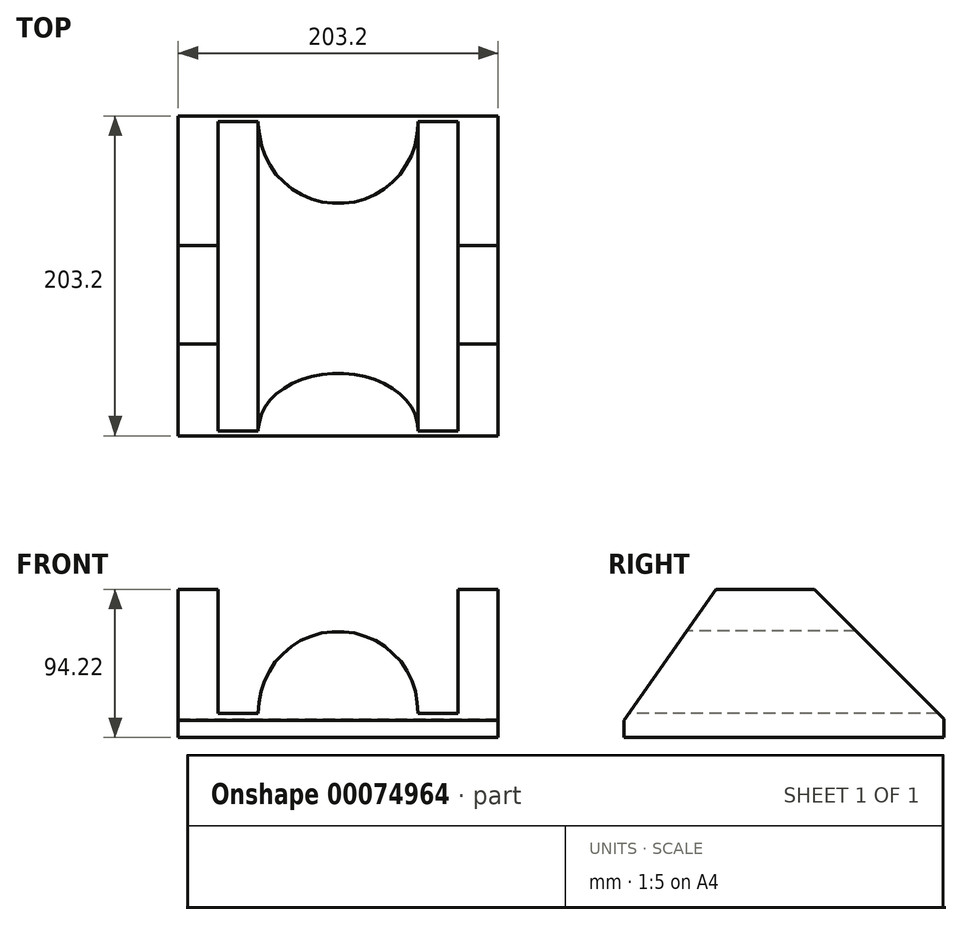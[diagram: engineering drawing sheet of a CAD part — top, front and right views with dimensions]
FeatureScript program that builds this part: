
annotation { "Feature Type Name" : "Feature", "Feature Type Description" : "" }
export const myFeature = defineFeature(function(context is Context, id is Id, definition is map)
    precondition{}
    {
        {
            var Q0;
            Q0=qCreatedBy(makeId("Front.planeOp"),FACE);
            var sketch = newSketch(context, id + "F0", { "sketchPlane" : qUnion([Q0])});
            skLineSegment(sketch, "E0.rect.top", {"start": v(101.6, -47.11) * mm, "end": v(-101.6, -47.11) * mm});
            skLineSegment(sketch, "E0.rect.left", {"start": v(101.6, 47.11) * mm, "end": v(101.6, -47.11) * mm});
            skLineSegment(sketch, "E0.rect.right", {"start": v(-101.6, 47.11) * mm, "end": v(-101.6, -47.11) * mm});
            skPoint(sketch, "E0.rect.middle", {"position": v(0, 0) * mm});
            skLineSegment(sketch, "E1", {"start": v(-101.6, 47.11) * mm, "end": v(-76.2, 47.11) * mm});
            skLineSegment(sketch, "E2", {"start": v(101.6, 47.11) * mm, "end": v(76.2, 47.11) * mm});
            skLineSegment(sketch, "E3", {"start": v(-101.6, -47.11) * mm, "end": v(-101.6, -31.87) * mm});
            skLineSegment(sketch, "E4", {"start": v(-76.2, 47.11) * mm, "end": v(-76.2, -31.87) * mm});
            skLineSegment(sketch, "E5", {"start": v(76.2, -31.75) * mm, "end": v(76.2, 47.11) * mm});
            skPoint(sketch, "E6", {"position": v(0, -31.75) * mm});
            skPoint(sketch, "E7", {"position": v(-50.8, -31.87) * mm});
            skPoint(sketch, "E8", {"position": v(-25.4, -31.75) * mm});
            skPoint(sketch, "E9", {"position": v(50.8, -31.75) * mm});
            skArc(sketch, "E10", {"start": v(50.8, -31.75) * mm, "mid": v(-0.06, 20.57) * mm, "end": v(-50.8, -31.87) * mm});
            skLineSegment(sketch, "E11", {"start": v(-76.2, -31.87) * mm, "end": v(-50.8, -31.87) * mm});
            skLineSegment(sketch, "E12", {"start": v(50.8, -31.75) * mm, "end": v(76.2, -31.75) * mm});
            skSolve(sketch);
        }
        {
            var Q0;
            Q0=makeQuery(id+"F0.imprint","IMPRINT",FACE,{"disambiguationData":[TD([[makeQuery(id+"F0.imprint","IMPRINT",EDGE,{"derivedFrom":sQuery(id+"F0.wireOp",EDGE,"E0.rect.top")}),-1.0]])]});
            extrude(context, id + "F1", {"entities" : qUnion([Q0]), "oppositeDirection" : true, "depth" : 203.2 * mm});
        }
        {
            var Q0;
            Q0=makeQuery(id+"F1.opExtrude","CAP_FACE",FACE,{"disambiguationData":[OSD([sQuery(id+"F0.wireOp",EDGE,"E0.rect.top"),sQuery(id+"F0.wireOp",EDGE,"E0.rect.left"),sQuery(id+"F0.wireOp",EDGE,"E0.rect.right"),sQuery(id+"F0.wireOp",EDGE,"E1"),sQuery(id+"F0.wireOp",EDGE,"E2"),sQuery(id+"F0.wireOp",EDGE,"E3"),sQuery(id+"F0.wireOp",EDGE,"E4"),sQuery(id+"F0.wireOp",EDGE,"E5"),sQuery(id+"F0.wireOp",EDGE,"E10"),sQuery(id+"F0.wireOp",EDGE,"E11"),sQuery(id+"F0.wireOp",EDGE,"E12")])],"isStart":true});
            var Q1;
            Q1=makeQuery(id+"F1.opExtrude","CAP_EDGE",EDGE,{"disambiguationData":[OSD([sQuery(id+"F0.wireOp",EDGE,"E11")])],"isStart":true});
            cPlane(context, id + "F2", {"entities" : qUnion([Q0, Q1]), "cplaneType" : CPlaneType.LINE_ANGLE, "offset" : 152.4 * mm, "angle" : 145 * degree, "width" : 152.4 * mm, "height" : 152.4 * mm});
        }
        {
            var Q0;
            Q0=qCreatedBy(id+"F2.planeOp",FACE);
            var sketch = newSketch(context, id + "F3", { "sketchPlane" : qUnion([Q0])});
            skLineSegment(sketch, "E13.rect.bottom", {"start": v(121.97, -105.4) * mm, "end": v(-121.97, -105.4) * mm});
            skLineSegment(sketch, "E13.rect.top", {"start": v(121.97, 131.24) * mm, "end": v(-121.97, 131.24) * mm});
            skLineSegment(sketch, "E13.rect.left", {"start": v(121.97, -105.4) * mm, "end": v(121.97, 131.24) * mm});
            skLineSegment(sketch, "E13.rect.right", {"start": v(-121.97, -105.4) * mm, "end": v(-121.97, 131.24) * mm});
            skPoint(sketch, "E13.rect.middle", {"position": v(0, 12.91) * mm});
            skSolve(sketch);
        }
        {
            var Q0;
            Q0=makeQuery(id+"F3.imprint","IMPRINT",FACE,{"disambiguationData":[TD([[makeQuery(id+"F3.imprint","IMPRINT",EDGE,{"derivedFrom":sQuery(id+"F3.wireOp",EDGE,"E13.rect.bottom")}),-1.0]])]});
            extrude(context, id + "F4", {"entities" : qUnion([Q0]), "operationType" : NewBodyOperationType.REMOVE, "depth" : 50.8 * mm});
        }
        {
            var Q0;
            Q0=qCreatedBy(id+"F2.planeOp",FACE);
            var sketch = newSketch(context, id + "F5", { "sketchPlane" : qUnion([Q0])});
            skLineSegment(sketch, "E14.rect.bottom", {"start": v(119.92, -92.4) * mm, "end": v(-119.92, -92.4) * mm});
            skLineSegment(sketch, "E14.rect.top", {"start": v(119.92, 116.73) * mm, "end": v(-119.92, 116.73) * mm});
            skLineSegment(sketch, "E14.rect.left", {"start": v(119.92, -92.4) * mm, "end": v(119.92, 116.73) * mm});
            skLineSegment(sketch, "E14.rect.right", {"start": v(-119.92, -92.4) * mm, "end": v(-119.92, 116.73) * mm});
            skPoint(sketch, "E14.rect.middle", {"position": v(0, 12.16) * mm});
            skSolve(sketch);
        }
        {
            var Q0;
            Q0=makeQuery(id+"F5.imprint","IMPRINT",FACE,{"disambiguationData":[TD([[makeQuery(id+"F5.imprint","IMPRINT",EDGE,{"derivedFrom":sQuery(id+"F5.wireOp",EDGE,"E14.rect.bottom")}),-1.0]])]});
            extrude(context, id + "F6", {"entities" : qUnion([Q0]), "operationType" : NewBodyOperationType.REMOVE, "oppositeDirection" : true, "depth" : 2.54 * mm});
        }
        {
            var Q0;
            Q0=makeQuery(id+"F1.opExtrude","CAP_FACE",FACE,{"disambiguationData":[OSD([sQuery(id+"F0.wireOp",EDGE,"E0.rect.top"),sQuery(id+"F0.wireOp",EDGE,"E0.rect.left"),sQuery(id+"F0.wireOp",EDGE,"E0.rect.right"),sQuery(id+"F0.wireOp",EDGE,"E1"),sQuery(id+"F0.wireOp",EDGE,"E2"),sQuery(id+"F0.wireOp",EDGE,"E3"),sQuery(id+"F0.wireOp",EDGE,"E4"),sQuery(id+"F0.wireOp",EDGE,"E5"),sQuery(id+"F0.wireOp",EDGE,"E10"),sQuery(id+"F0.wireOp",EDGE,"E11"),sQuery(id+"F0.wireOp",EDGE,"E12")])],"isStart":false});
            var Q1;
            Q1=makeQuery(id+"F1.opExtrude","CAP_EDGE",EDGE,{"disambiguationData":[OSD([sQuery(id+"F0.wireOp",EDGE,"E12")])],"isStart":false});
            cPlane(context, id + "F7", {"entities" : qUnion([Q0, Q1]), "cplaneType" : CPlaneType.LINE_ANGLE, "offset" : 152.4 * mm, "angle" : 45 * degree, "width" : 152.4 * mm, "height" : 152.4 * mm});
        }
        {
            var Q0;
            Q0=qCreatedBy(id+"F7.planeOp",FACE);
            var sketch = newSketch(context, id + "F8", { "sketchPlane" : qUnion([Q0])});
            skLineSegment(sketch, "E15.rect.bottom", {"start": v(-124.8, -225.08) * mm, "end": v(124.8, -225.08) * mm});
            skLineSegment(sketch, "E15.rect.top", {"start": v(-124.8, 16.6) * mm, "end": v(124.8, 16.6) * mm});
            skLineSegment(sketch, "E15.rect.left", {"start": v(-124.8, -225.08) * mm, "end": v(-124.8, 16.6) * mm});
            skLineSegment(sketch, "E15.rect.right", {"start": v(124.8, -225.08) * mm, "end": v(124.8, 16.6) * mm});
            skPoint(sketch, "E15.rect.middle", {"position": v(0, -104.24) * mm});
            skSolve(sketch);
        }
        {
            var Q0;
            Q0=makeQuery(id+"F8.imprint","IMPRINT",FACE,{"disambiguationData":[TD([[makeQuery(id+"F8.imprint","IMPRINT",EDGE,{"derivedFrom":sQuery(id+"F8.wireOp",EDGE,"E15.rect.bottom")}),1.0]])]});
            extrude(context, id + "F9", {"entities" : qUnion([Q0]), "operationType" : NewBodyOperationType.REMOVE, "oppositeDirection" : true, "depth" : 76.2 * mm});
        }
        {
            var Q0;
            Q0=qCreatedBy(id+"F7.planeOp",FACE);
            var sketch = newSketch(context, id + "F10", { "sketchPlane" : qUnion([Q0])});
            skLineSegment(sketch, "E16.rect.bottom", {"start": v(-110.24, -207.12) * mm, "end": v(110.24, -207.12) * mm});
            skLineSegment(sketch, "E16.rect.top", {"start": v(-110.24, 0.95) * mm, "end": v(110.24, 0.95) * mm});
            skLineSegment(sketch, "E16.rect.left", {"start": v(-110.24, -207.12) * mm, "end": v(-110.24, 0.95) * mm});
            skLineSegment(sketch, "E16.rect.right", {"start": v(110.24, -207.12) * mm, "end": v(110.24, 0.95) * mm});
            skPoint(sketch, "E16.rect.middle", {"position": v(0, -103.08) * mm});
            skSolve(sketch);
        }
        {
            var Q0;
            Q0=makeQuery(id+"F10.imprint","IMPRINT",FACE,{"disambiguationData":[TD([[makeQuery(id+"F10.imprint","IMPRINT",EDGE,{"derivedFrom":sQuery(id+"F10.wireOp",EDGE,"E16.rect.bottom")}),1.0]])]});
            extrude(context, id + "F11", {"entities" : qUnion([Q0]), "operationType" : NewBodyOperationType.REMOVE, "depth" : 2.54 * mm});
        }
    });
